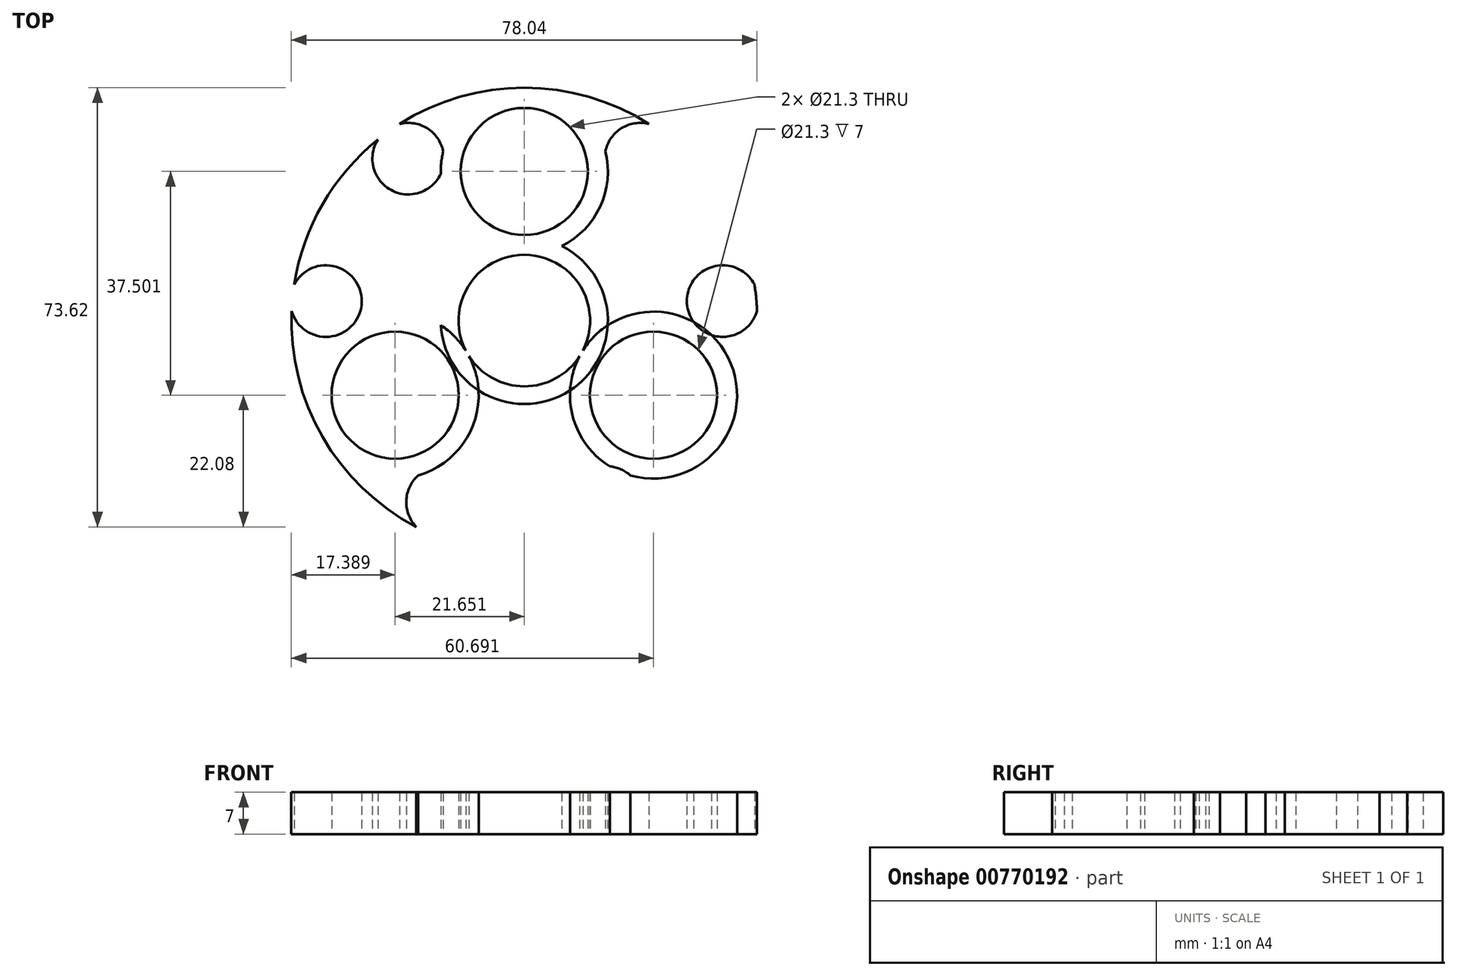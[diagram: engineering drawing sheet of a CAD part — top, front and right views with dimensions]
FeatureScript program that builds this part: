
annotation { "Feature Type Name" : "Feature", "Feature Type Description" : "" }
export const myFeature = defineFeature(function(context is Context, id is Id, definition is map)
    precondition{}
    {
        {
            var Q0;
            Q0=qCreatedBy(makeId("Top.planeOp"),FACE);
            var sketch = newSketch(context, id + "F0", { "sketchPlane" : qUnion([Q0])});
            skCircle(sketch, "E0", {"center": v(0, 0) * mm, "radius": 11.03 * mm});
            skCircle(sketch, "E1", {"center": v(0, 0) * mm, "radius": 14 * mm});
            skCircle(sketch, "E2", {"center": v(0, 25) * mm, "radius": 10.65 * mm});
            skCircle(sketch, "E3", {"center": v(0, 25) * mm, "radius": 14 * mm});
            skCircle(sketch, "E4.1.2", {"center": v(-21.65, -12.5) * mm, "radius": 14 * mm});
            skCircle(sketch, "E4.1.3", {"center": v(-21.65, -12.5) * mm, "radius": 10.65 * mm});
            skCircle(sketch, "E4.2.2", {"center": v(21.65, -12.5) * mm, "radius": 14 * mm});
            skCircle(sketch, "E4.2.3", {"center": v(21.65, -12.5) * mm, "radius": 10.65 * mm});
            skCircle(sketch, "E5", {"center": v(0, 0) * mm, "radius": 39.04 * mm});
            skCircle(sketch, "E6", {"center": v(-19.46, 27.15) * mm, "radius": 6 * mm});
            skCircle(sketch, "E7.MirrorC", {"center": v(19.46, 27.15) * mm, "radius": 6 * mm});
            skCircle(sketch, "E8.1.0", {"center": v(-13.78, -30.42) * mm, "radius": 6 * mm});
            skCircle(sketch, "E8.1.1", {"center": v(-33.24, 3.28) * mm, "radius": 6 * mm});
            skCircle(sketch, "E8.2.0", {"center": v(33.24, 3.28) * mm, "radius": 6 * mm});
            skCircle(sketch, "E8.2.1", {"center": v(13.78, -30.42) * mm, "radius": 6 * mm});
            skSolve(sketch);
        }
        {
            var Q0;
            {var subQ0=sQuery(id+"F0.wireOp",EDGE,"E6");var subQ1=sQuery(id+"F0.wireOp",EDGE,"E3");var subQ2=makeQuery(id+"F0.imprint","INTERSECT",VERTEX,{"disambiguationData":[OD(0.0)],"derivedFrom":[subQ1,subQ0]});Q0=makeQuery(id+"F0.imprint","IMPRINT",FACE,{"disambiguationData":[TD([[makeQuery(id+"F0.imprint","IMPRINT",EDGE,{"disambiguationData":[TD([[subQ2,1.0]])],"derivedFrom":subQ1}),-1.0]])]});}
            var Q1;
            {var subQ0=sQuery(id+"F0.wireOp",EDGE,"E8.1.0");var subQ1=sQuery(id+"F0.wireOp",EDGE,"E4.1.2");var subQ2=makeQuery(id+"F0.imprint","INTERSECT",VERTEX,{"disambiguationData":[OD(0.0)],"derivedFrom":[subQ1,subQ0]});Q1=makeQuery(id+"F0.imprint","IMPRINT",FACE,{"disambiguationData":[TD([[makeQuery(id+"F0.imprint","IMPRINT",EDGE,{"disambiguationData":[TD([[subQ2,1.0]])],"derivedFrom":subQ1}),-1.0]])]});}
            var Q2;
            {var subQ0=sQuery(id+"F0.wireOp",EDGE,"E8.2.0");var subQ1=sQuery(id+"F0.wireOp",EDGE,"E4.2.2");var subQ2=makeQuery(id+"F0.imprint","INTERSECT",VERTEX,{"disambiguationData":[OD(0.0)],"derivedFrom":[subQ1,subQ0]});Q2=makeQuery(id+"F0.imprint","IMPRINT",FACE,{"disambiguationData":[TD([[makeQuery(id+"F0.imprint","IMPRINT",EDGE,{"disambiguationData":[TD([[subQ2,1.0]])],"derivedFrom":subQ1}),-1.0]])]});}
            var Q3;
            Q3=makeQuery(id+"F0.imprint","IMPRINT",FACE,{"disambiguationData":[TD([[makeQuery(id+"F0.imprint","IMPRINT",EDGE,{"derivedFrom":sQuery(id+"F0.wireOp",EDGE,"E2")}),-1.0]])]});
            var Q4;
            {var subQ0=sQuery(id+"F0.wireOp",EDGE,"E0");var subQ1=sQuery(id+"F0.wireOp",EDGE,"E3");var subQ2=makeQuery(id+"F0.imprint","INTERSECT",VERTEX,{"disambiguationData":[OD(1.0)],"derivedFrom":[subQ1,subQ0]});Q4=makeQuery(id+"F0.imprint","IMPRINT",FACE,{"disambiguationData":[TD([[makeQuery(id+"F0.imprint","IMPRINT",EDGE,{"disambiguationData":[TD([[subQ2,-1.0]])],"derivedFrom":subQ1}),-1.0]])]});}
            var Q5;
            {var subQ0=sQuery(id+"F0.wireOp",EDGE,"E1");var subQ1=sQuery(id+"F0.wireOp",EDGE,"E3");var subQ2=makeQuery(id+"F0.imprint","INTERSECT",VERTEX,{"disambiguationData":[OD(0.0)],"derivedFrom":[subQ1,subQ0]});Q5=makeQuery(id+"F0.imprint","IMPRINT",FACE,{"disambiguationData":[TD([[makeQuery(id+"F0.imprint","IMPRINT",EDGE,{"disambiguationData":[TD([[subQ2,-1.0]])],"derivedFrom":subQ1}),-1.0]])]});}
            var Q6;
            {var subQ0=sQuery(id+"F0.wireOp",EDGE,"E1");var subQ1=sQuery(id+"F0.wireOp",EDGE,"E4.1.2");var subQ2=makeQuery(id+"F0.imprint","INTERSECT",VERTEX,{"disambiguationData":[OD(0.0)],"derivedFrom":[subQ1,subQ0]});Q6=makeQuery(id+"F0.imprint","IMPRINT",FACE,{"disambiguationData":[TD([[makeQuery(id+"F0.imprint","IMPRINT",EDGE,{"disambiguationData":[TD([[subQ2,-1.0]])],"derivedFrom":subQ1}),1.0]])]});}
            var Q7;
            {var subQ0=sQuery(id+"F0.wireOp",EDGE,"E1");var subQ1=sQuery(id+"F0.wireOp",EDGE,"E4.1.2");var subQ2=makeQuery(id+"F0.imprint","INTERSECT",VERTEX,{"disambiguationData":[OD(0.0)],"derivedFrom":[subQ1,subQ0]});Q7=makeQuery(id+"F0.imprint","IMPRINT",FACE,{"disambiguationData":[TD([[makeQuery(id+"F0.imprint","IMPRINT",EDGE,{"disambiguationData":[TD([[subQ2,-1.0]])],"derivedFrom":subQ1}),-1.0]])]});}
            var Q8;
            {var subQ0=sQuery(id+"F0.wireOp",EDGE,"E1");var subQ1=sQuery(id+"F0.wireOp",EDGE,"E3");var subQ2=makeQuery(id+"F0.imprint","INTERSECT",VERTEX,{"disambiguationData":[OD(0.0)],"derivedFrom":[subQ1,subQ0]});Q8=makeQuery(id+"F0.imprint","IMPRINT",FACE,{"disambiguationData":[TD([[makeQuery(id+"F0.imprint","IMPRINT",EDGE,{"disambiguationData":[TD([[subQ2,-1.0]])],"derivedFrom":subQ1}),1.0]])]});}
            var Q9;
            {var subQ0=sQuery(id+"F0.wireOp",EDGE,"E4.2.2");var subQ1=sQuery(id+"F0.wireOp",EDGE,"E1");var subQ2=makeQuery(id+"F0.imprint","INTERSECT",VERTEX,{"disambiguationData":[OD(0.0)],"derivedFrom":[subQ1,subQ0]});Q9=makeQuery(id+"F0.imprint","IMPRINT",FACE,{"disambiguationData":[TD([[makeQuery(id+"F0.imprint","IMPRINT",EDGE,{"disambiguationData":[TD([[subQ2,1.0]])],"derivedFrom":subQ1}),1.0]])]});}
            var Q10;
            Q10=makeQuery(id+"F0.imprint","IMPRINT",FACE,{"disambiguationData":[TD([[makeQuery(id+"F0.imprint","IMPRINT",EDGE,{"derivedFrom":sQuery(id+"F0.wireOp",EDGE,"E4.2.3")}),-1.0]])]});
            var Q11;
            Q11=makeQuery(id+"F0.imprint","IMPRINT",FACE,{"disambiguationData":[TD([[makeQuery(id+"F0.imprint","IMPRINT",EDGE,{"derivedFrom":sQuery(id+"F0.wireOp",EDGE,"E4.1.3")}),-1.0]])]});
            var Q12;
            {var subQ0=sQuery(id+"F0.wireOp",EDGE,"E8.1.1");var subQ1=sQuery(id+"F0.wireOp",EDGE,"E4.1.2");var subQ2=makeQuery(id+"F0.imprint","INTERSECT",VERTEX,{"disambiguationData":[OD(0.0)],"derivedFrom":[subQ1,subQ0]});Q12=makeQuery(id+"F0.imprint","IMPRINT",FACE,{"disambiguationData":[TD([[makeQuery(id+"F0.imprint","IMPRINT",EDGE,{"disambiguationData":[TD([[subQ2,1.0]])],"derivedFrom":subQ1}),1.0]])]});}
            var Q13;
            {var subQ0=sQuery(id+"F0.wireOp",EDGE,"E6");var subQ1=sQuery(id+"F0.wireOp",EDGE,"E3");var subQ2=makeQuery(id+"F0.imprint","INTERSECT",VERTEX,{"disambiguationData":[OD(0.0)],"derivedFrom":[subQ1,subQ0]});Q13=makeQuery(id+"F0.imprint","IMPRINT",FACE,{"disambiguationData":[TD([[makeQuery(id+"F0.imprint","IMPRINT",EDGE,{"disambiguationData":[TD([[subQ2,-1.0]])],"derivedFrom":subQ1}),1.0]])]});}
            var Q14;
            {var subQ0=sQuery(id+"F0.wireOp",EDGE,"E7.MirrorC");var subQ1=sQuery(id+"F0.wireOp",EDGE,"E3");var subQ2=makeQuery(id+"F0.imprint","INTERSECT",VERTEX,{"disambiguationData":[OD(0.0)],"derivedFrom":[subQ1,subQ0]});Q14=makeQuery(id+"F0.imprint","IMPRINT",FACE,{"disambiguationData":[TD([[makeQuery(id+"F0.imprint","IMPRINT",EDGE,{"disambiguationData":[TD([[subQ2,1.0]])],"derivedFrom":subQ1}),1.0]])]});}
            var Q15;
            {var subQ0=sQuery(id+"F0.wireOp",EDGE,"E8.2.0");var subQ1=sQuery(id+"F0.wireOp",EDGE,"E4.2.2");var subQ2=makeQuery(id+"F0.imprint","INTERSECT",VERTEX,{"disambiguationData":[OD(0.0)],"derivedFrom":[subQ1,subQ0]});Q15=makeQuery(id+"F0.imprint","IMPRINT",FACE,{"disambiguationData":[TD([[makeQuery(id+"F0.imprint","IMPRINT",EDGE,{"disambiguationData":[TD([[subQ2,-1.0]])],"derivedFrom":subQ1}),1.0]])]});}
            var Q16;
            {var subQ0=sQuery(id+"F0.wireOp",EDGE,"E8.2.1");var subQ1=sQuery(id+"F0.wireOp",EDGE,"E4.2.2");var subQ2=makeQuery(id+"F0.imprint","INTERSECT",VERTEX,{"disambiguationData":[OD(0.0)],"derivedFrom":[subQ1,subQ0]});Q16=makeQuery(id+"F0.imprint","IMPRINT",FACE,{"disambiguationData":[TD([[makeQuery(id+"F0.imprint","IMPRINT",EDGE,{"disambiguationData":[TD([[subQ2,1.0]])],"derivedFrom":subQ1}),1.0]])]});}
            var Q17;
            {var subQ0=sQuery(id+"F0.wireOp",EDGE,"E8.1.0");var subQ1=sQuery(id+"F0.wireOp",EDGE,"E4.1.2");var subQ2=makeQuery(id+"F0.imprint","INTERSECT",VERTEX,{"disambiguationData":[OD(0.0)],"derivedFrom":[subQ1,subQ0]});Q17=makeQuery(id+"F0.imprint","IMPRINT",FACE,{"disambiguationData":[TD([[makeQuery(id+"F0.imprint","IMPRINT",EDGE,{"disambiguationData":[TD([[subQ2,-1.0]])],"derivedFrom":subQ1}),1.0]])]});}
            extrude(context, id + "F1", {"entities" : qUnion([Q0, Q1, Q2, Q3, Q4, Q5, Q6, Q7, Q8, Q9, Q10, Q11, Q12, Q13, Q14, Q15, Q16, Q17]), "depth" : 7 * mm, "offsetDistance" : 25 * mm});
        }
    });
